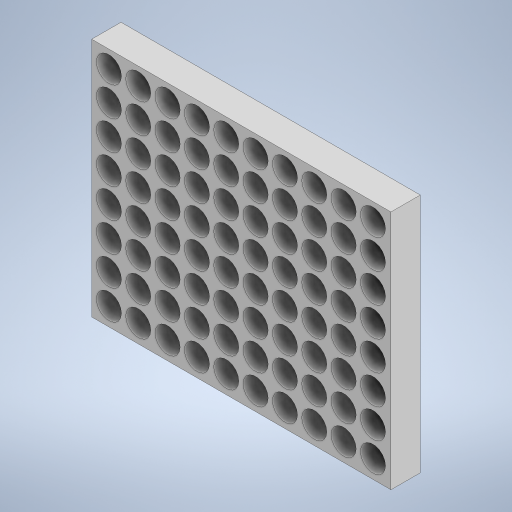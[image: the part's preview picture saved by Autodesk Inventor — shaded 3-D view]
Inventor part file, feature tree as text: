
AUTODESK INVENTOR PART (.ipt)
format: ipt  version: 2024 (Build 280153000, 153)  size: 470,016 bytes
history: native  units: in
note: dims shown in document units (in); Inventor stores cm internally (conversion verified against a paired STEP export)
features: extrude x2, sketch x2, projected_geometry x1
ambient origin geometry x8: Origin, YZ Plane, XZ Plane, XY Plane, X Axis, Y Axis, Z Axis, Center Point
bodies: Solid1 (feature_tree)
feature tree (5):
  extrude  "Extrusion1"  Depth=1.0in
  extrude  "Extrusion2"  Depth=1.0in TaperAngle=0.0deg
  sketch  "Sketch1"  dims[d0=10.2in d4=3.1496in d6=1.0in d7=3.937in d9=1.0in]
  sketch  "Sketch2"  dims[d12=8.2in d13=1.0in d14=0.0in d15=0.587in d16=0.587in d17=0.855in d18=3.1496in d20=1.0in d21=3.937in d23=1.0in d26=0.0in d27=0.0in d28=0.855in]
  projected_geometry  "Projected Loop1"
